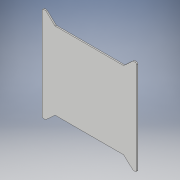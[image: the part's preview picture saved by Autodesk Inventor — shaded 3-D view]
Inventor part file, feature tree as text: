
AUTODESK INVENTOR PART (.ipt)
format: ipt  version: 2017 (Build 210142000, 142)  size: 125,952 bytes
history: native  units: in
note: dims shown in document units (in); Inventor stores cm internally (conversion verified against a paired STEP export)
features: extrude x2, sketch x2, fillet x1, projected_geometry x1
ambient origin geometry x8: Origin, YZ Plane, XZ Plane, XY Plane, X Axis, Y Axis, Z Axis, Center Point
bodies: Solid1 (feature_tree)
feature tree (6):
  extrude  "Extrusion1"  Depth=8.5827in
  fillet  "Fillet1"  Radius=0.1181in
  extrude  "Extrusion2"  Depth=0.7874in
  sketch  "Sketch1"  dims[d0=8.5827in d1=8.5827in d2=0.1181in d3=0.0in]
  sketch  "Sketch2"  dims[d4=0.125in d5=0.7874in d6=1.1811in d7=1.1811in d8=0.7874in d9=0.1969in d10=0.1969in d11=0.1181in d12=0.0in]
  projected_geometry  "Projected Loop1"
